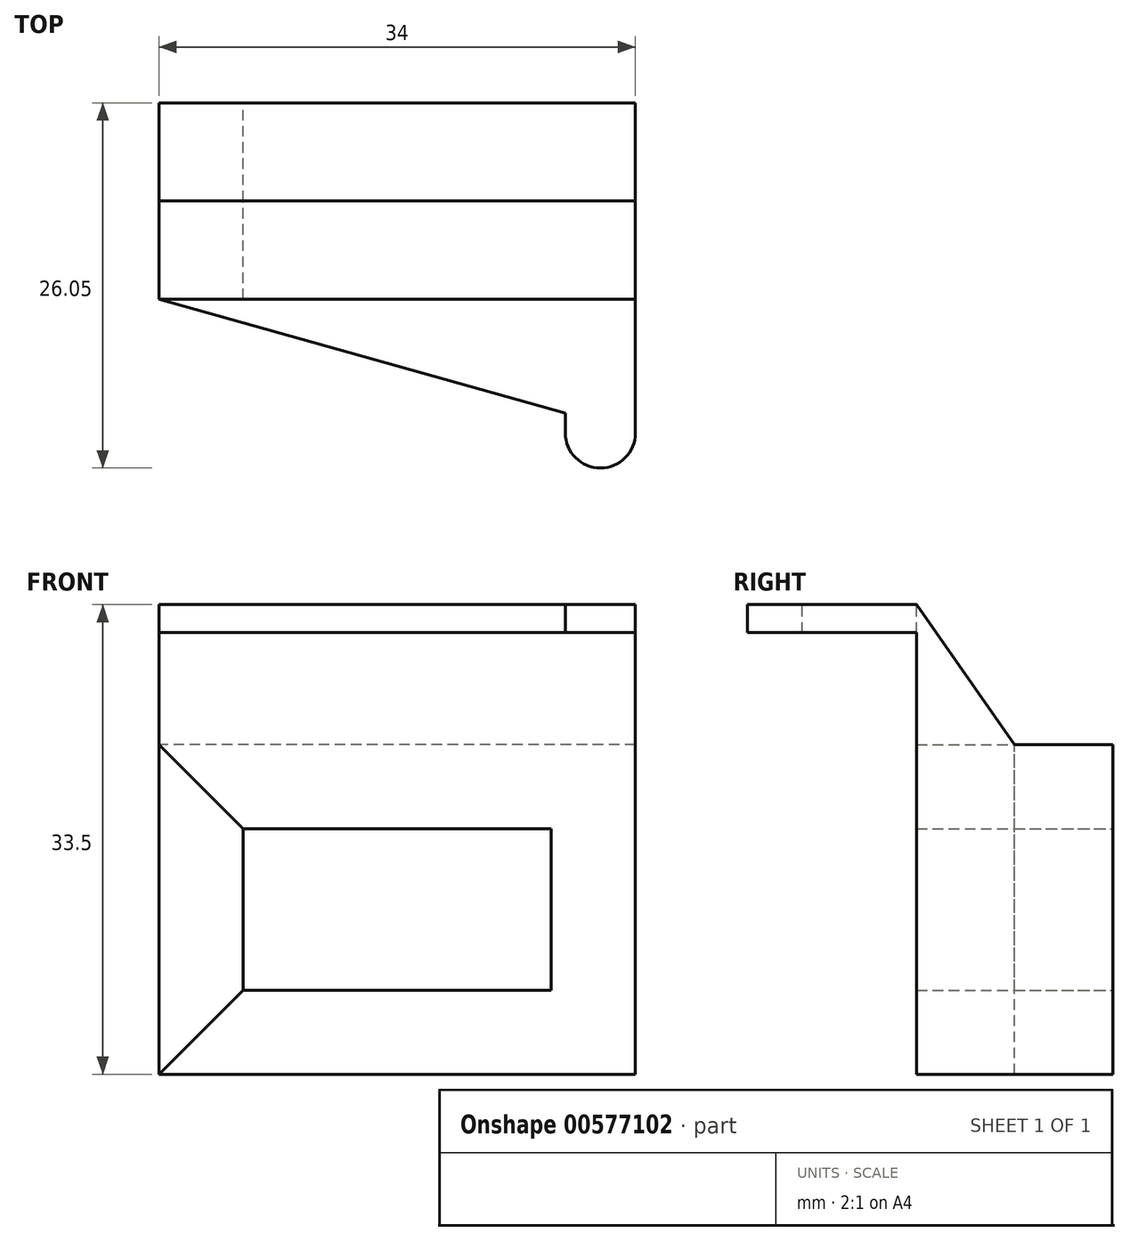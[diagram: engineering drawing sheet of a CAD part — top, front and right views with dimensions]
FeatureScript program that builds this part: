
annotation { "Feature Type Name" : "Feature", "Feature Type Description" : "" }
export const myFeature = defineFeature(function(context is Context, id is Id, definition is map)
    precondition{}
    {
        {
            var Q0;
            Q0=qCreatedBy(makeId("Front.planeOp"),FACE);
            var sketch = newSketch(context, id + "F0", { "sketchPlane" : qUnion([Q0])});
            skLineSegment(sketch, "E0.bottom", {"start": v(0, 0) * mm, "end": v(34, 0) * mm});
            skLineSegment(sketch, "E0.top", {"start": v(0, 23.5) * mm, "end": v(34, 23.5) * mm});
            skLineSegment(sketch, "E0.left", {"start": v(0, 0) * mm, "end": v(0, 23.5) * mm});
            skLineSegment(sketch, "E0.right", {"start": v(34, 0) * mm, "end": v(34, 23.5) * mm});
            skLineSegment(sketch, "E1.bottom", {"start": v(6, 6) * mm, "end": v(28, 6) * mm});
            skLineSegment(sketch, "E1.top", {"start": v(6, 17.5) * mm, "end": v(28, 17.5) * mm});
            skLineSegment(sketch, "E1.left", {"start": v(6, 6) * mm, "end": v(6, 17.5) * mm});
            skLineSegment(sketch, "E1.right", {"start": v(28, 6) * mm, "end": v(28, 17.5) * mm});
            skSolve(sketch);
        }
        {
            var Q0;
            Q0=makeQuery(id+"F0.imprint","IMPRINT",FACE,{"disambiguationData":[TD([[makeQuery(id+"F0.imprint","IMPRINT",EDGE,{"derivedFrom":sQuery(id+"F0.wireOp",EDGE,"E0.bottom")}),1.0]])]});
            extrude(context, id + "F1", {"entities" : qUnion([Q0]), "depth" : 7 * mm, "offsetDistance" : 25 * mm});
        }
        {
            var Q0;
            Q0=makeQuery(id+"F1.opExtrude","CAP_FACE",FACE,{"disambiguationData":[OSD([sQuery(id+"F0.wireOp",EDGE,"E0.bottom"),sQuery(id+"F0.wireOp",EDGE,"E0.top"),sQuery(id+"F0.wireOp",EDGE,"E0.left"),sQuery(id+"F0.wireOp",EDGE,"E0.right"),sQuery(id+"F0.wireOp",EDGE,"E1.bottom"),sQuery(id+"F0.wireOp",EDGE,"E1.top"),sQuery(id+"F0.wireOp",EDGE,"E1.left"),sQuery(id+"F0.wireOp",EDGE,"E1.right")])],"isStart":false});
            var sketch = newSketch(context, id + "F2", { "sketchPlane" : qUnion([Q0])});
            skLineSegment(sketch, "E2", {"start": v(6, 17.5) * mm, "end": v(0, 23.5) * mm});
            skLineSegment(sketch, "E3", {"start": v(0, 23.5) * mm, "end": v(34, 23.5) * mm});
            skLineSegment(sketch, "E4", {"start": v(34, 23.5) * mm, "end": v(34, 0) * mm});
            skLineSegment(sketch, "E5", {"start": v(34, 0) * mm, "end": v(0, 0) * mm});
            skLineSegment(sketch, "E6", {"start": v(0, 0) * mm, "end": v(6, 6) * mm});
            skLineSegment(sketch, "E7", {"start": v(6, 6) * mm, "end": v(6, 17.5) * mm});
            skSolve(sketch);
        }
        {
            var Q0;
            Q0=makeQuery(id+"F2.imprint","IMPRINT",FACE,{"disambiguationData":[TD([[makeQuery(id+"F2.imprint","IMPRINT",EDGE,{"derivedFrom":sQuery(id+"F2.wireOp",EDGE,"E2")}),-1.0]])]});
            extrude(context, id + "F3", {"entities" : qUnion([Q0]), "operationType" : NewBodyOperationType.ADD, "depth" : 7 * mm, "offsetDistance" : 25 * mm});
        }
        {
            var Q0;
            Q0=makeQuery(id+"F3.boolean.opBoolean","MERGE",FACE,{"derivedFrom":[makeQuery(id+"F1.opExtrude","SWEPT_FACE",FACE,{"disambiguationData":[OSD([sQuery(id+"F0.wireOp",EDGE,"E0.top")])]}),makeQuery(id+"F3.opExtrude","SWEPT_FACE",FACE,{"disambiguationData":[OSD([sQuery(id+"F2.wireOp",EDGE,"E3")])]})]});
            cPlane(context, id + "F4", {"entities" : qUnion([Q0]), "cplaneType" : CPlaneType.OFFSET, "offset" : 10 * mm, "width" : 150 * mm, "height" : 150 * mm});
        }
        {
            var Q0;
            Q0=qCreatedBy(id+"F4.planeOp",FACE);
            var sketch = newSketch(context, id + "F5", { "sketchPlane" : qUnion([Q0])});
            skPoint(sketch, "E8.0", {"position": v(0, -7) * mm});
            skLineSegment(sketch, "E9.right", {"start": v(34, -14) * mm, "end": v(34, -23.55) * mm});
            skLineSegment(sketch, "E10", {"start": v(0, -14) * mm, "end": v(29, -22.15) * mm});
            skArc(sketch, "E11", {"start": v(29, -23.55) * mm, "mid": v(31.5, -26.05) * mm, "end": v(34, -23.55) * mm});
            skPoint(sketch, "E11.second.point", {"position": v(29, -23.55) * mm});
            skPoint(sketch, "E11.third.point", {"position": v(30.88, -25.97) * mm});
            skLineSegment(sketch, "E12", {"start": v(29, -23.55) * mm, "end": v(29, -22.15) * mm});
            skLineSegment(sketch, "E13", {"start": v(34, -23.55) * mm, "end": v(31.5, -23.55) * mm, "construction": true});
            skLineSegment(sketch, "E14", {"start": v(29, -23.55) * mm, "end": v(31.5, -23.55) * mm, "construction": true});
            skLineSegment(sketch, "E15", {"start": v(0, -14) * mm, "end": v(34, -14) * mm});
            skSolve(sketch);
        }
        {
            var Q0;
            Q0=makeQuery(id+"F5.imprint","IMPRINT",FACE,{"disambiguationData":[TD([[makeQuery(id+"F5.imprint","IMPRINT",EDGE,{"derivedFrom":sQuery(id+"F5.wireOp",EDGE,"E9.right")}),-1.0]])]});
            extrude(context, id + "F6", {"entities" : qUnion([Q0]), "oppositeDirection" : true, "depth" : 2 * mm, "offsetDistance" : 25 * mm});
        }
        {
            var Q0;
            Q0=makeQuery(id+"F1.opExtrude","SWEPT_FACE",FACE,{"disambiguationData":[OSD([sQuery(id+"F0.wireOp",EDGE,"E0.left")])]});
            var sketch = newSketch(context, id + "F7", { "sketchPlane" : qUnion([Q0])});
            skPoint(sketch, "E16.0", {"position": v(14, 33.5) * mm});
            skLineSegment(sketch, "E17", {"start": v(7, 23.5) * mm, "end": v(14, 33.5) * mm});
            skLineSegment(sketch, "E18", {"start": v(14, 23.5) * mm, "end": v(7, 23.5) * mm});
            skLineSegment(sketch, "E19", {"start": v(14, 23.5) * mm, "end": v(14, 33.5) * mm});
            skSolve(sketch);
        }
        {
            var Q0;
            Q0=makeQuery(id+"F7.imprint","IMPRINT",FACE,{"disambiguationData":[TD([[makeQuery(id+"F7.imprint","IMPRINT",EDGE,{"derivedFrom":sQuery(id+"F7.wireOp",EDGE,"E17")}),-1.0]])]});
            extrude(context, id + "F8", {"entities" : qUnion([Q0]), "operationType" : NewBodyOperationType.ADD, "oppositeDirection" : true, "depth" : 34 * mm, "offsetDistance" : 25 * mm});
        }
        {
            var Q0;
            Q0=makeQuery(id+"F3.opExtrude","CAP_EDGE",EDGE,{"disambiguationData":[OSD([sQuery(id+"F0.wireOp",EDGE,"E1.right")])],"isStart":false});
            cPoint(context, id + "F9", {"entities" : qUnion([Q0]), "parameter" : 0.5});
        }
        {
            var Q0;
            Q0=makeQuery(id+"F1.opExtrude","CAP_EDGE",EDGE,{"disambiguationData":[OSD([sQuery(id+"F0.wireOp",EDGE,"E1.right")])],"isStart":true});
            cPoint(context, id + "F10", {"entities" : qUnion([Q0]), "parameter" : 0.5});
        }
        {
            var Q0;
            Q0=makeQuery(id+"F1.opExtrude","CAP_EDGE",EDGE,{"disambiguationData":[OSD([sQuery(id+"F0.wireOp",EDGE,"E0.left")])],"isStart":false});
            cPoint(context, id + "F11", {"entities" : qUnion([Q0]), "parameter" : 0.5});
        }
        {
            var Q0;
            Q0 = qCreatedBy(id + "F9" ,VERTEX);
            var Q1;
            Q1 = qCreatedBy(id + "F10" ,VERTEX);
            var Q2;
            Q2 = qCreatedBy(id + "F11" ,VERTEX);
            cPlane(context, id + "F12", {"entities" : qUnion([Q0, Q1, Q2]), "cplaneType" : CPlaneType.THREE_POINT, "offset" : 25 * mm, "width" : 150 * mm, "height" : 150 * mm});
        }
    });
